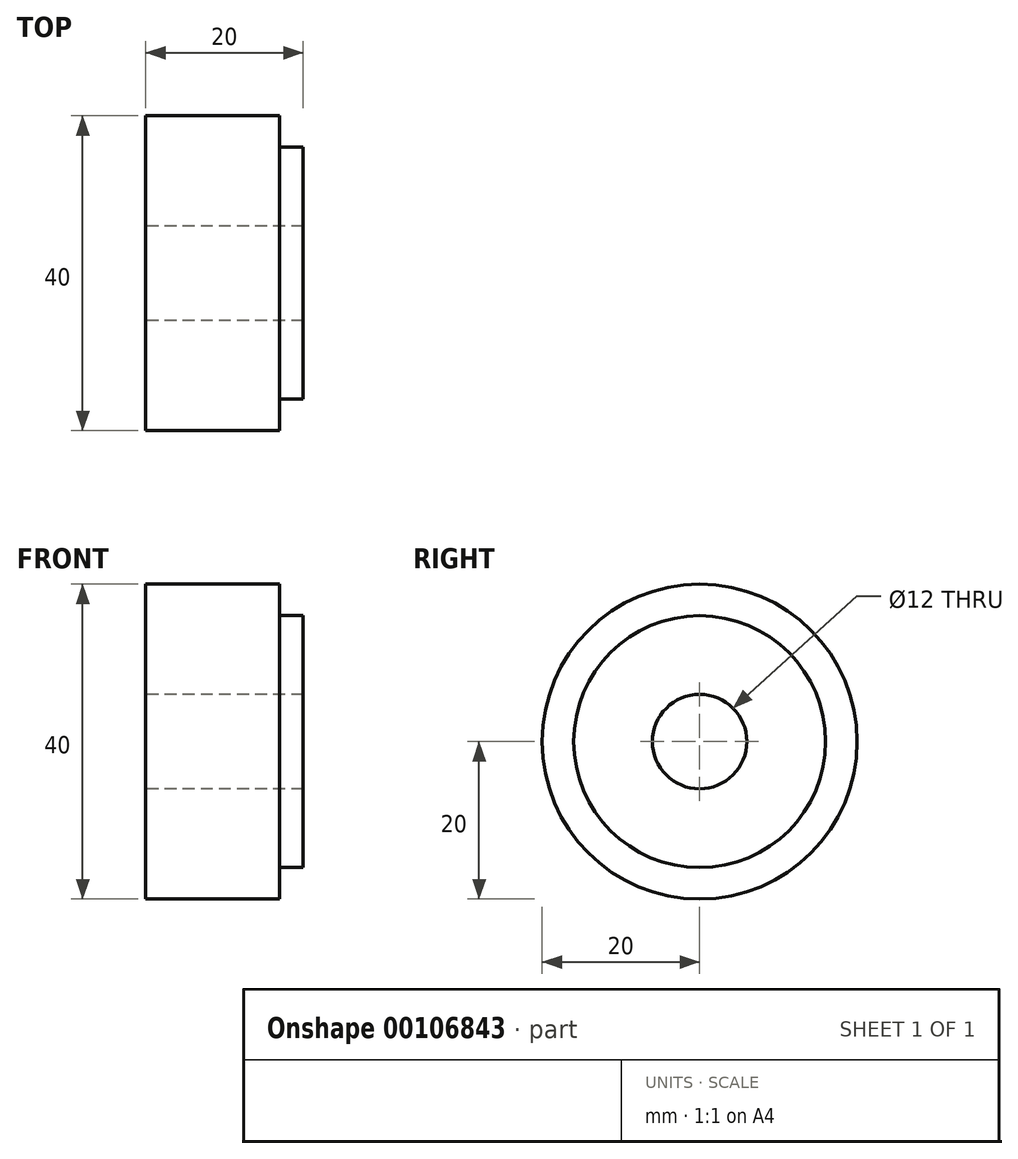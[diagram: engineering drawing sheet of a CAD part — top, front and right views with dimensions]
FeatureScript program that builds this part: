
annotation { "Feature Type Name" : "Feature", "Feature Type Description" : "" }
export const myFeature = defineFeature(function(context is Context, id is Id, definition is map)
    precondition{}
    {
        {
            var Q0;
            Q0=qCreatedBy(makeId("Front.planeOp"),FACE);
            var sketch = newSketch(context, id + "F0", { "sketchPlane" : qUnion([Q0])});
            skLineSegment(sketch, "E0.bottom", {"start": v(0, 6) * mm, "end": v(3, 6) * mm});
            skLineSegment(sketch, "E0.top", {"start": v(0, 16) * mm, "end": v(3, 16) * mm});
            skLineSegment(sketch, "E0.left", {"start": v(0, 6) * mm, "end": v(0, 16) * mm});
            skLineSegment(sketch, "E0.right", {"start": v(3, 6) * mm, "end": v(3, 16) * mm});
            skLineSegment(sketch, "E1", {"start": v(0, 0) * mm, "end": v(53.38, 0) * mm, "construction": true});
            skSolve(sketch);
        }
        {
            var Q0;
            Q0=makeQuery(id+"F0.imprint","IMPRINT",FACE,{"disambiguationData":[TD([[makeQuery(id+"F0.imprint","IMPRINT",EDGE,{"derivedFrom":sQuery(id+"F0.wireOp",EDGE,"E0.bottom")}),1.0]])]});
            var Q1;
            Q1=sQuery(id+"F0.wireOp",EDGE,"E1");
            revolve(context, id + "F1", {"entities" : qUnion([Q0]), "axis" : qUnion([Q1]), "revolveType" : RevolveType.FULL});
        }
        {
            var Q0;
            Q0=qCreatedBy(makeId("Front.planeOp"),FACE);
            var sketch = newSketch(context, id + "F2", { "sketchPlane" : qUnion([Q0])});
            skLineSegment(sketch, "E2.bottom", {"start": v(0, 6) * mm, "end": v(-17, 6) * mm});
            skLineSegment(sketch, "E2.top", {"start": v(0, 20) * mm, "end": v(-17, 20) * mm});
            skLineSegment(sketch, "E2.left", {"start": v(0, 6) * mm, "end": v(0, 20) * mm});
            skLineSegment(sketch, "E2.right", {"start": v(-17, 6) * mm, "end": v(-17, 20) * mm});
            skSolve(sketch);
        }
        {
            var Q0;
            Q0=makeQuery(id+"F2.imprint","IMPRINT",FACE,{"disambiguationData":[TD([[makeQuery(id+"F2.imprint","IMPRINT",EDGE,{"derivedFrom":sQuery(id+"F2.wireOp",EDGE,"E2.bottom")}),-1.0]])]});
            var Q1;
            Q1 = qSketchRegion(id + "F0", true);
            var Q2;
            Q2=sQuery(id+"F0.wireOp",EDGE,"E1");
            revolve(context, id + "F3", {"operationType" : NewBodyOperationType.ADD, "entities" : qUnion([Q0, Q1]), "axis" : qUnion([Q2]), "revolveType" : RevolveType.FULL});
        }
    });
